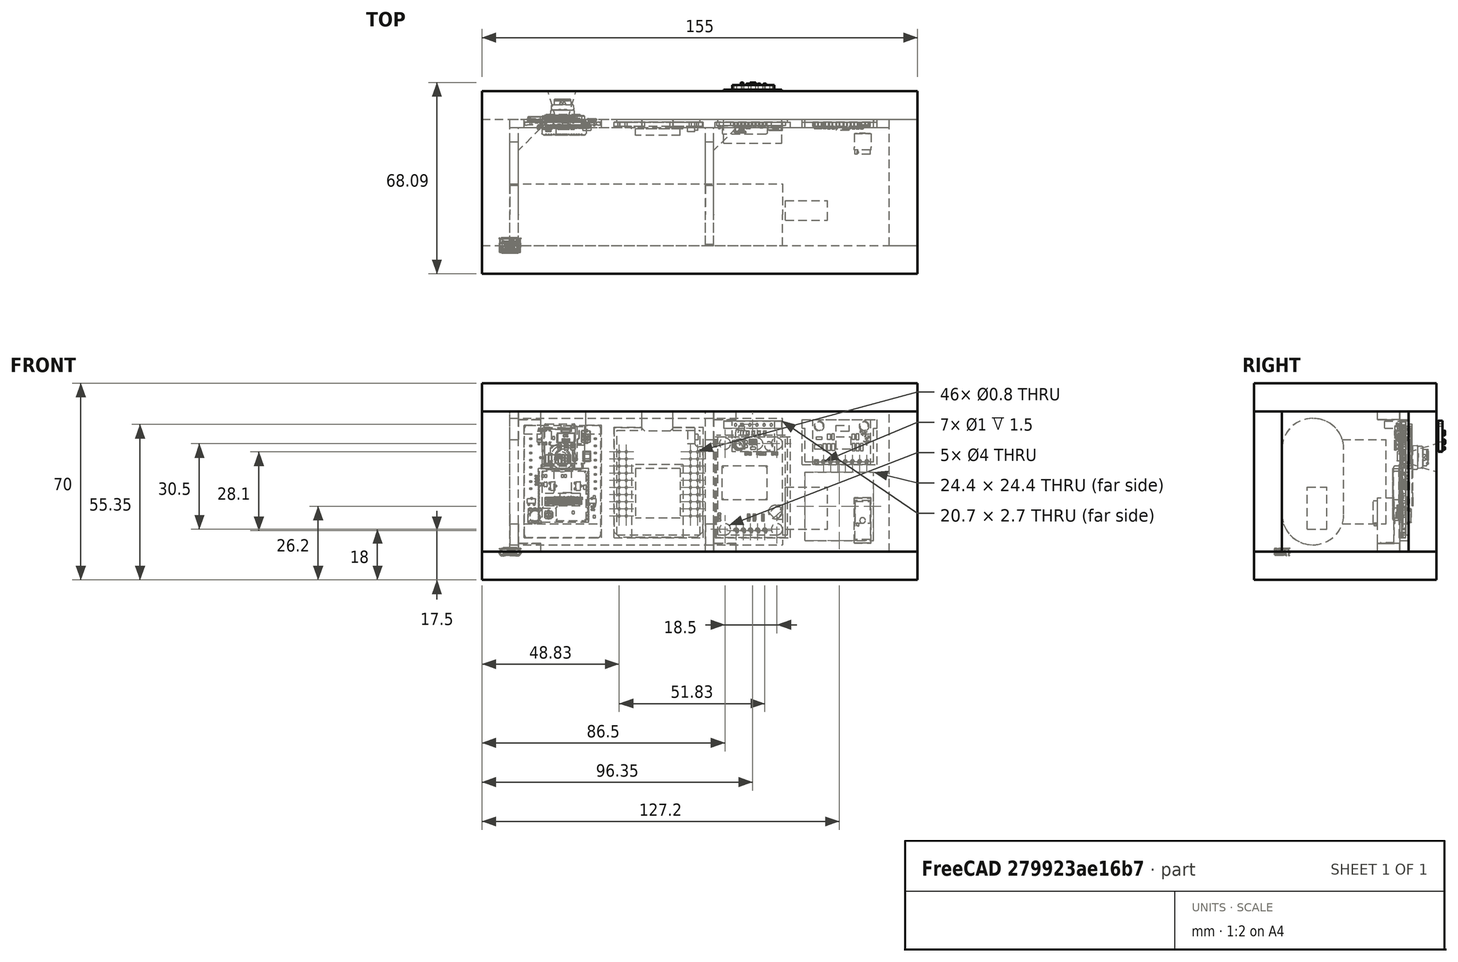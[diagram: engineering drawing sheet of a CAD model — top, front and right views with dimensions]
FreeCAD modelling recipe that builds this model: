
FCSTD DOCUMENT  (FreeCAD 0.18R4 (GitTag))
Label: fli3d chicken
License: All rights reserved
LicenseURL: http://en.wikipedia.org/wiki/All_rights_reserved
objects: Part::Feature×145, Part::Cylinder×138, Part::Cut×54, Part::Box×49, Part::Compound×15, Part::MultiFuse×13, Part::Chamfer×6, Part::Fillet×5, Mesh::Feature×4, App::Part×1, Part::Cone×1
note: 426 computed .brp shape members not serialized (recipe doc carries the construction recipe); baked Part::Feature solids carry a one-line shape summary decoded from their .brp

FEATURE [Part::Feature] Part__Feature183  label="pcb"
  shape: bbox 20.5 x 16 x 1.5 mm, 92 faces (baked)
FEATURE [Part::Feature] Part__Feature184  label="pcb001"
  shape: bbox 5.2 x 4.498 x 1 mm, 6 faces (baked)
FEATURE [Part::Feature] Part__Feature185  label="pcb002"
  shape: bbox 4.542 x 2.102 x 1.5 mm, 6 faces (baked)
FEATURE [Part::Feature] Part__Feature186  label="pcb003"
  shape: bbox 1.036 x 2.536 x 1 mm, 6 faces (baked)
FEATURE [Part::Feature] Part__Feature187  label="pcb004"
  shape: bbox 0.9209 x 2 x 1 mm, 6 faces (baked)
FEATURE [Part::Feature] Part__Feature188  label="pcb005"
  shape: bbox 1 x 2 x 1 mm, 6 faces (baked)
FEATURE [Part::Feature] Part__Feature189  label="pcb006"
  shape: bbox 1.036 x 2.536 x 1 mm, 6 faces (baked)
FEATURE [Part::Feature] Part__Feature190  label="pcb007"
  shape: bbox 1 x 2 x 1 mm, 6 faces (baked)
FEATURE [Part::Feature] Part__Feature191  label="pcb008"
  shape: bbox 2 x 1 x 1 mm, 6 faces (baked)
FEATURE [Part::Feature] Part__Feature192  label="pcb009"
  shape: bbox 1.036 x 2.536 x 1 mm, 6 faces (baked)
FEATURE [Part::Feature] Part__Feature193  label="pcb010"
  shape: bbox 1.036 x 2.536 x 1 mm, 6 faces (baked)
FEATURE [Part::Feature] Part__Feature194  label="pcb011"
  shape: bbox 0.9209 x 2 x 1 mm, 6 faces (baked)
FEATURE [Part::Feature] Part__Feature195  label="pcb012"
  shape: bbox 1.036 x 2.536 x 1 mm, 6 faces (baked)
FEATURE [Part::Feature] Part__Feature196  label="pcb013"
  shape: bbox 1.036 x 2.536 x 1 mm, 6 faces (baked)
FEATURE [Part::Feature] Part__Feature197  label="pcb014"
  shape: bbox 2.769 x 1.403 x 1 mm, 6 faces (baked)
FEATURE [Part::Feature] Part__Feature198  label="pcb015"
  shape: bbox 1.5 x 1.5 x 1.5 mm, 4 faces (baked)
FEATURE [Part::Feature] Part__Feature199  label="pcb016"
  shape: bbox 1.5 x 1.5 x 1.5 mm, 4 faces (baked)
FEATURE [Part::Feature] Part__Feature200  label="pcb017"
  shape: bbox 1.5 x 1.5 x 1.5 mm, 7 faces (baked)
FEATURE [Part::Feature] Part__Feature201  label="pcb018"
  shape: bbox 1.5 x 1.5 x 1.5 mm, 4 faces (baked)
FEATURE [Part::Feature] Part__Feature202  label="pcb019"
  shape: bbox 3.5 x 3.5 x 1.5 mm, 4 faces (baked)
FEATURE [Part::Feature] Part__Feature203  label="pcb020"
  shape: bbox 1.5 x 1.5 x 1.5 mm, 4 faces (baked)
FEATURE [Part::Feature] Part__Feature204  label="pcb021"
  shape: bbox 1.5 x 1.5 x 1.5 mm, 4 faces (baked)
FEATURE [Part::Feature] Part__Feature205  label="pcb022"
  shape: bbox 1.5 x 1.5 x 1.5 mm, 4 faces (baked)
FEATURE [Part::Feature] Part__Feature206  label="pcb023"
  shape: bbox 1.5 x 1.5 x 1.5 mm, 4 faces (baked)
FEATURE [Part::Feature] Part__Feature207  label="pcb024"
  shape: bbox 3.5 x 3.5 x 1.5 mm, 4 faces (baked)
FEATURE [Part::Feature] Part__Feature208  label="pcb025"
  shape: bbox 0.9 x 0.9 x 0.5 mm, 14 faces (baked)
FEATURE [Part::Feature] Part__Feature209  label="pcb026"
  shape: bbox 2.8 x 2.123 x 0.5 mm, 26 faces (baked)
FEATURE [Part::Feature] Part__Feature210  label="pcb027"
  shape: bbox 2.123 x 2.8 x 0.5 mm, 26 faces (baked)
FEATURE [Part::Feature] Part__Feature211  label="pcb028"
  shape: bbox 0.9 x 0.9 x 0.5 mm, 11 faces (baked)
FEATURE [Part::Compound] Compound019  label="MPU6050"
  Links = -> [Part__Feature183,Part__Feature184,Part__Feature185,Part__Feature186,Part__Feature187,Part__Feature188,Part__Feature189,Part__Feature190,Part__Feature191,Part__Feature192,Part__Feature193,Part__Feature194,Part__Feature195,Part__Feature196,Part__Feature197,Part__Feature198,Part__Feature199,Part__Feature200,Part__Feature201,Part__Feature202,Part__Feature203,Part__Feature204,Part__Feature205,+6 more]
  Placement = pos=(118,42.5,39) rot=(1,0,0;1.5708rad)
FEATURE [Part::Feature] Part__Feature251  label="Compound028"
  shape: bbox 0.9 x 0.55 x 1.7 mm, 36 faces (baked)
FEATURE [Part::Feature] Part__Feature252  label="Compound047"
  shape: bbox 0.9 x 0.55 x 1.7 mm, 36 faces (baked)
FEATURE [Part::Feature] Part__Feature253  label="Compound030"
  shape: bbox 1.7 x 0.9 x 0.9 mm, 34 faces (baked)
FEATURE [Part::Feature] Part__Feature255  label="Compound048"
  shape: bbox 0.9 x 0.55 x 1.7 mm, 36 faces (baked)
FEATURE [Part::Feature] Part__Feature257  label="Compound050"
  shape: bbox 2.518 x 0.974 x 2.018 mm, 265 faces (baked)
FEATURE [Part::Feature] Part__Feature258  label="Compound051"
  shape: bbox 0.9 x 0.9 x 1.7 mm, 34 faces (baked)
FEATURE [Part::Feature] Part__Feature259  label="Compound052"
  shape: bbox 0.9 x 0.55 x 1.7 mm, 36 faces (baked)
FEATURE [Part::Feature] Part__Feature262  label="Compound055"
  shape: bbox 15 x 1.57 x 11 mm, 14 faces (baked)
FEATURE [Part::Compound] Compound021  label="BMP280"
  Links = -> [Part__Feature262,Part__Feature255,Part__Feature258,Part__Feature259,Part__Feature257,Part__Feature252,Part__Feature251,Part__Feature253]
  Placement = pos=(90,80,45) rot=(0,1,0;3.14159rad)
FEATURE [Part::Feature] Part__Feature327  label="Pin Header 4 x 1 TH 2.54mm Pitch v033"
  Placement = pos=(4.72,-2.66216,2.20216) rot=(0.57735,0.57735,0.57735;4.18879rad)
  shape: bbox 0.635 x 11.43 x 0.635 mm, 14 faces (baked)
FEATURE [Mesh::Feature] __54_pin_header008  label="2.54_pin_header008"
  Placement = pos=(8.5,27.2,-0.8) rot=(0,0,1;0rad)
FEATURE [Part::Feature] Part__Feature328  label="Pin Header 4 x 1 TH 2.54mm Pitch v034"
  Placement = pos=(14.89,-2.66216,25.2022) rot=(0.57735,0.57735,0.57735;4.18879rad)
  shape: bbox 0.635 x 11.43 x 0.635 mm, 14 faces (baked)
FEATURE [Part::Feature] Part__Feature329  label="Pin Header 4 x 1 TH 2.54mm Pitch v035"
  Placement = pos=(4.72,-2.66216,2.20216) rot=(0.57735,0.57735,0.57735;4.18879rad)
  shape: bbox 0.635 x 11.43 x 0.635 mm, 14 faces (baked)
FEATURE [Part::Feature] Part__Feature330  label="Pin Header 4 x 1 TH 2.54mm Pitch v036"
  Placement = pos=(14.89,-2.66216,25.2022) rot=(0.57735,0.57735,0.57735;4.18879rad)
  shape: bbox 0.635 x 11.43 x 0.635 mm, 14 faces (baked)
FEATURE [Part::Feature] Part__Feature331  label="Pin Header 4 x 1 TH 2.54mm Pitch v037"
  Placement = pos=(4.72,-2.66216,2.20216) rot=(0.57735,0.57735,0.57735;4.18879rad)
  shape: bbox 0.635 x 11.43 x 0.635 mm, 14 faces (baked)
FEATURE [Part::Feature] Part__Feature332  label="Pin Header 4 x 1 TH 2.54mm Pitch v038"
  Placement = pos=(14.883,-2.66216,2.20216) rot=(0.57735,0.57735,0.57735;4.18879rad)
  shape: bbox 0.635 x 11.43 x 0.635 mm, 14 faces (baked)
FEATURE [Part::Feature] Part__Feature333  label="Pin Header 4 x 1 TH 2.54mm Pitch v039"
  Placement = pos=(14.89,-2.66216,25.2022) rot=(0.57735,0.57735,0.57735;4.18879rad)
  shape: bbox 0.635 x 11.43 x 0.635 mm, 14 faces (baked)
FEATURE [Part::Feature] Part__Feature334  label="Pin Header 4 x 1 TH 2.54mm Pitch v040"
  Placement = pos=(14.89,-2.66216,25.2022) rot=(0.57735,0.57735,0.57735;4.18879rad)
  shape: bbox 0.635 x 11.43 x 0.635 mm, 14 faces (baked)
FEATURE [Part::Feature] Part__Feature335  label="Pin Header 4 x 1 TH 2.54mm Pitch v041"
  Placement = pos=(4.72,-2.66216,2.20216) rot=(0.57735,0.57735,0.57735;4.18879rad)
  shape: bbox 0.635 x 11.43 x 0.635 mm, 14 faces (baked)
FEATURE [Part::Feature] Part__Feature336  label="Pin Header 4 x 1 TH 2.54mm Pitch v042"
  Placement = pos=(4.71,-2.66216,25.2022) rot=(-0.57735,-0.57735,-0.57735;2.0944rad)
  shape: bbox 0.635 x 11.43 x 0.635 mm, 14 faces (baked)
FEATURE [Part::Feature] Part__Feature337  label="Pin Header 4 x 1 TH 2.54mm Pitch v043"
  Placement = pos=(4.71,-2.66216,25.2022) rot=(-0.57735,-0.57735,-0.57735;2.0944rad)
  shape: bbox 0.635 x 11.43 x 0.635 mm, 14 faces (baked)
FEATURE [Part::Feature] Part__Feature338  label="Pin Header 4 x 1 TH 2.54mm Pitch v044"
  Placement = pos=(14.883,-2.66216,2.20216) rot=(0.57735,0.57735,0.57735;4.18879rad)
  shape: bbox 0.635 x 11.43 x 0.635 mm, 14 faces (baked)
FEATURE [Part::Feature] Part__Feature339  label="Pin Header 4 x 1 TH 2.54mm Pitch v045"
  Placement = pos=(14.883,-2.66216,2.20216) rot=(0.57735,0.57735,0.57735;4.18879rad)
  shape: bbox 0.635 x 11.43 x 0.635 mm, 14 faces (baked)
FEATURE [Part::Feature] Part__Feature340  label="Pin Header 4 x 1 TH 2.54mm Pitch v046"
  Placement = pos=(14.883,-2.66216,2.20216) rot=(0.57735,0.57735,0.57735;4.18879rad)
  shape: bbox 0.635 x 11.43 x 0.635 mm, 14 faces (baked)
FEATURE [Part::Feature] Part__Feature341  label="u005"
  Placement = pos=(30.5196,-1.14548,7.21031) rot=(1,0,0;3.14159rad)
  shape: bbox 1.8 x 0.165 x 0.4527 mm, 9 faces (baked)
FEATURE [Part::Feature] Part__Feature342  label="u006"
  Placement = pos=(30.5196,-1.14548,7.21031) rot=(1,0,0;3.14159rad)
  shape: bbox 0.5465 x 0.165 x 0.6 mm, 7 faces (baked)
FEATURE [Part::Feature] Part__Feature343  label="switch-3x4x2mm - 2 Pad v002"
  Placement = pos=(4,0.684989,21.7704) rot=(1,0,0;1.5708rad)
  shape: bbox 5.004 x 1.93 x 2.997 mm, 237 faces (baked)
FEATURE [Part::Feature] Part__Feature344  label="Pin Header 4 x 1 TH 2.54mm Pitch v047"
  Placement = pos=(4.71,-2.66216,25.2022) rot=(-0.57735,-0.57735,-0.57735;2.0944rad)
  shape: bbox 0.635 x 11.43 x 0.635 mm, 14 faces (baked)
FEATURE [Part::Feature] Part__Feature345  label="nano - reg001"
  Placement = pos=(4.45,-0.0046987,14.7657) rot=(-0.707107,0,0.707107;3.14159rad)
  shape: bbox 8.304 x 1.695 x 6.504 mm, 194 faces (baked)
FEATURE [Part::Feature] Part__Feature346  label="Pin Header 4 x 1 TH 2.54mm Pitch v048"
  Placement = pos=(4.71,-2.66216,25.2022) rot=(-0.57735,-0.57735,-0.57735;2.0944rad)
  shape: bbox 0.635 x 11.43 x 0.635 mm, 14 faces (baked)
FEATURE [Part::Compound] Compound121  label="pins001"
  Links = -> [Part__Feature344,Part__Feature340,Part__Feature332,Part__Feature337,Part__Feature334,Part__Feature346,Part__Feature339,Part__Feature330,Part__Feature328,Part__Feature338,Part__Feature335,Part__Feature336,Part__Feature329,Part__Feature327,Part__Feature331,Part__Feature333]
FEATURE [Part::Feature] Part__Feature347  label="u007"
  Placement = pos=(30.5196,-1.14548,7.21031) rot=(1,0,0;3.14159rad)
  shape: bbox 1.8 x 0.165 x 0.4527 mm, 9 faces (baked)
FEATURE [Part::Feature] Part__Feature348  label="u008"
  Placement = pos=(30.5196,-1.14548,7.21031) rot=(1,0,0;3.14159rad)
  shape: bbox 2.616 x 1.25 x 2.633 mm, 39 faces (baked)
FEATURE [Part::Feature] Part__Feature349  label="u009"
  Placement = pos=(30.5196,-1.14548,7.21031) rot=(1,0,0;3.14159rad)
  shape: bbox 0.5465 x 0.165 x 0.6 mm, 7 faces (baked)
FEATURE [Part::Feature] Part__Feature350  label="SOLID004"
  Placement = pos=(15.3712,-0.145481,22.8712) rot=(0.707107,0,-0.707107;3.14159rad)
  shape: bbox 19.24 x 3.435 x 18.07 mm, 845 faces (baked)
FEATURE [Part::Feature] Part__Feature351  label="capacitor-CAPM-TANTB-YL v004"
  Placement = pos=(11,0.104975,22.105) rot=(1,0,0;1.5708rad)
  shape: bbox 3.446 x 2.076 x 3.006 mm, 54 faces (baked)
FEATURE [Part::Feature] Part__Feature352  label="capacitor-CAPM-TANTB-YL v005"
  Placement = pos=(11,0.104975,22.105) rot=(1,0,0;1.5708rad)
  shape: bbox 1 x 1.13 x 2.2 mm, 18 faces (baked)
FEATURE [Part::Feature] Part__Feature353  label="capacitor-CAPM-TANTB-YL v006"
  Placement = pos=(11,0.104975,22.105) rot=(1,0,0;1.5708rad)
  shape: bbox 1 x 1.13 x 2.2 mm, 18 faces (baked)
FEATURE [Part::Feature] Part__Feature354  label="resistor-NTC-0402-T0.6 v021"
  Placement = pos=(10.2,0,12.3) rot=(0,1,0;1.5708rad)
  shape: bbox 0.6 x 0.55 x 1.1 mm, 42 faces (baked)
FEATURE [Part::Feature] Part__Feature355  label="Component009"
  Placement = pos=(4,-1.3e-14,7) rot=(0.57735,-0.57735,0.57735;2.0944rad)
  shape: bbox 1 x 1.05 x 0.4 mm, 14 faces (baked)
FEATURE [Part::Feature] Part__Feature356  label="Component5(Mirror)004"
  Placement = pos=(4,-1.2e-14,8.27) rot=(0.57735,0.57735,0.57735;4.18879rad)
  shape: bbox 1 x 1.05 x 0.4 mm, 14 faces (baked)
FEATURE [Part::Feature] Part__Feature357  label="icbody001"
  Placement = pos=(4,-1.3e-14,7) rot=(0.57735,-0.57735,0.57735;2.0944rad)
  shape: bbox 3.9 x 1.45 x 4.9 mm, 50 faces (baked)
FEATURE [Part::Feature] Part__Feature358  label="Component010"
  Placement = pos=(4,-1.5e-14,5.73) rot=(0.57735,-0.57735,0.57735;2.0944rad)
  shape: bbox 1 x 1.05 x 0.4 mm, 14 faces (baked)
FEATURE [Part::Feature] Part__Feature359  label="Component5(Mirror)005"
  Placement = pos=(4,-1.3e-14,7) rot=(0.57735,0.57735,0.57735;4.18879rad)
  shape: bbox 1 x 1.05 x 0.4 mm, 14 faces (baked)
FEATURE [Part::Feature] Part__Feature360  label="Component5(Mirror)006"
  Placement = pos=(4,-1.6e-14,4.46) rot=(0.57735,0.57735,0.57735;4.18879rad)
  shape: bbox 1 x 1.05 x 0.4 mm, 14 faces (baked)
FEATURE [Part::Feature] Part__Feature361  label="Component011"
  Placement = pos=(4,-1.6e-14,4.46) rot=(0.57735,-0.57735,0.57735;2.0944rad)
  shape: bbox 1 x 1.05 x 0.4 mm, 14 faces (baked)
FEATURE [Part::Feature] Part__Feature362  label="Component5(Mirror)007"
  Placement = pos=(4,-1.5e-14,5.73) rot=(0.57735,0.57735,0.57735;4.18879rad)
  shape: bbox 1 x 1.05 x 0.4 mm, 14 faces (baked)
FEATURE [Part::Feature] Part__Feature363  label="Fusion054"
  Placement = pos=(12,-5e-15,18) rot=(0.57735,-0.57735,0.57735;2.0944rad)
  shape: bbox 0.8 x 0.5 x 1.6 mm, 25 faces (baked)
FEATURE [Part::Feature] Part__Feature364  label="Fillet034"
  Placement = pos=(12,-5e-15,18) rot=(0.57735,-0.57735,0.57735;2.0944rad)
  shape: bbox 0.8 x 0.3 x 1.2 mm, 18 faces (baked)
FEATURE [Part::Feature] Part__Feature365  label="resistor-NTC-0402-T0.6 v022"
  Placement = pos=(12.2,0,15.8) rot=(0,1,0;1.5708rad)
  shape: bbox 0.6 x 0.55 x 1.1 mm, 42 faces (baked)
FEATURE [Part::Feature] Part__Feature366  label="Component012"
  Placement = pos=(4,-1.2e-14,8.27) rot=(0.57735,-0.57735,0.57735;2.0944rad)
  shape: bbox 1 x 1.05 x 0.4 mm, 14 faces (baked)
FEATURE [Part::Feature] Part__Feature367  label="smd-transistor-SOT23-3 v017"
  Placement = pos=(27,1.05803,23.942) rot=(-1,0,0;1.5708rad)
  shape: bbox 0.6498 x 0.8933 x 0.6 mm, 7 faces (baked)
FEATURE [Part::Feature] Part__Feature368  label="smd-transistor-SOT23-3 v018"
  Placement = pos=(27,1.05803,2.44197) rot=(-1,0,0;1.5708rad)
  shape: bbox 0.6498 x 0.8933 x 0.6 mm, 7 faces (baked)
FEATURE [Part::Feature] Part__Feature369  label="resistor-NTC-0402-T0.6 v023"
  Placement = pos=(25.5,0,24.5) rot=(0,0,1;0rad)
  shape: bbox 1.1 x 0.55 x 0.6 mm, 42 faces (baked)
FEATURE [Part::Feature] Part__Feature370  label="resistor-NTC-0402-T0.6 v024"
  Placement = pos=(28.5,0,24.5) rot=(0,0,1;0rad)
  shape: bbox 1.1 x 0.55 x 0.6 mm, 42 faces (baked)
FEATURE [Part::Feature] Part__Feature371  label="smd-transistor-SOT23-3 v019"
  Placement = pos=(27,1.05803,2.44197) rot=(-1,0,0;1.5708rad)
  shape: bbox 0.6498 x 0.8933 x 0.6 mm, 7 faces (baked)
FEATURE [Part::Feature] Part__Feature372  label="resistor-NTC-0402-T0.6 v025"
  Placement = pos=(32.5,0,24.5) rot=(0,0,1;0rad)
  shape: bbox 1.1 x 0.55 x 0.6 mm, 42 faces (baked)
FEATURE [Part::Feature] Part__Feature373  label="smd-transistor-SOT23-3 v020"
  Placement = pos=(27,1.05803,2.44197) rot=(-1,0,0;1.5708rad)
  shape: bbox 0.6498 x 0.8933 x 0.6 mm, 7 faces (baked)
FEATURE [Part::Feature] Part__Feature374  label="smd-transistor-SOT23-3 v021"
  Placement = pos=(27,1.05803,2.44197) rot=(-1,0,0;1.5708rad)
  shape: bbox 1.651 x 1.1 x 3 mm, 34 faces (baked)
FEATURE [Part::Feature] Part__Feature375  label="resistor-NTC-0402-T0.6 v026"
  Placement = pos=(4.5,0,10.6) rot=(0,1,0;3.14159rad)
  shape: bbox 1.1 x 0.55 x 0.6 mm, 42 faces (baked)
FEATURE [Part::Feature] Part__Feature376  label="smd-transistor-SOT23-3 v022"
  Placement = pos=(27,1.05803,23.942) rot=(-1,0,0;1.5708rad)
  shape: bbox 0.6498 x 0.8933 x 0.6 mm, 7 faces (baked)
FEATURE [Part::Feature] Part__Feature377  label="smd-transistor-SOT23-3 v023"
  Placement = pos=(27,1.05803,23.942) rot=(-1,0,0;1.5708rad)
  shape: bbox 0.6498 x 0.8933 x 0.6 mm, 7 faces (baked)
FEATURE [Part::Feature] Part__Feature378  label="resistor-NTC-0805-T1.3 v002"
  Placement = pos=(10.35,0,14.65) rot=(0,1,0;1.5708rad)
  shape: bbox 1.3 x 1.4 x 2.2 mm, 42 faces (baked)
FEATURE [Part::Feature] Part__Feature379  label="resistor-NTC-0402-T0.6 v027"
  Placement = pos=(11.2,0,5.97136) rot=(0,1,0;1.5708rad)
  shape: bbox 0.6 x 0.55 x 1.1 mm, 42 faces (baked)
FEATURE [Part::Feature] Part__Feature380  label="resistor-NTC-0402-T0.6 v028"
  Placement = pos=(17.7,1,4.3) rot=(0,1,0;1.5708rad)
  shape: bbox 0.6 x 0.55 x 1.1 mm, 42 faces (baked)
FEATURE [Part::Feature] Part__Feature381  label="resistor-NTC-0402-T0.6 v029"
  Placement = pos=(18.7,1,4.3) rot=(0,1,0;1.5708rad)
  shape: bbox 0.6 x 0.55 x 1.1 mm, 42 faces (baked)
FEATURE [Part::Feature] Part__Feature382  label="resistor-NTC-0402-T0.6 v030"
  Placement = pos=(21,1,5.2) rot=(0,0,1;0rad)
  shape: bbox 1.1 x 0.55 x 0.6 mm, 42 faces (baked)
FEATURE [Part::Feature] Part__Feature383  label="resistor-NTC-0402-T0.6 v031"
  Placement = pos=(29.3,1,24.3) rot=(0,-1,0;1.5708rad)
  shape: bbox 0.6 x 0.55 x 1.1 mm, 42 faces (baked)
FEATURE [Part::Feature] Part__Feature384  label="smd-transistor-SOT23-3 v024"
  Placement = pos=(27,1.05803,23.942) rot=(-1,0,0;1.5708rad)
  shape: bbox 1.651 x 1.1 x 3 mm, 34 faces (baked)
FEATURE [Part::Feature] Part__Feature385  label="resistor-NTC-0402-T0.6 v032"
  Placement = pos=(30.3,1,24.3) rot=(0,-1,0;1.5708rad)
  shape: bbox 0.6 x 0.55 x 1.1 mm, 42 faces (baked)
FEATURE [Part::Feature] Part__Feature386  label="resistor-NTC-0402-T0.6 v033"
  Placement = pos=(19.7,1,4.3) rot=(0,1,0;1.5708rad)
  shape: bbox 0.6 x 0.55 x 1.1 mm, 42 faces (baked)
FEATURE [Part::Feature] Part__Feature387  label="resistor-NTC-0402-T0.6 v034"
  Placement = pos=(20.7,1,4.3) rot=(0,1,0;1.5708rad)
  shape: bbox 0.6 x 0.55 x 1.1 mm, 42 faces (baked)
FEATURE [Part::Feature] Part__Feature388  label="resistor-NTC-0402-T0.6 v035"
  Placement = pos=(18,1,6.2) rot=(0,0,1;0rad)
  shape: bbox 1.1 x 0.55 x 0.6 mm, 42 faces (baked)
FEATURE [Part::Feature] Part__Feature389  label="resistor-NTC-0402-T0.6 v036"
  Placement = pos=(18,1,7.2) rot=(0,0,1;0rad)
  shape: bbox 1.1 x 0.55 x 0.6 mm, 42 faces (baked)
FEATURE [Part::Feature] Part__Feature390  label="capacitor-CAPC-0603-T0.9-BN v003"
  Placement = pos=(21,1,7) rot=(0,0,1;0rad)
  shape: bbox 1.7 x 0.9 x 0.9 mm, 42 faces (baked)
FEATURE [Part::Feature] Part__Feature391  label="LED SMD 5050 White v002"
  Placement = pos=(30,1.2963,2.10027) rot=(-1,0,0;1.5708rad)
  shape: bbox 5.4 x 1.62 x 5 mm, 76 faces (baked)
FEATURE [Part::Feature] Part__Feature392  label="resistor-NTC-0402-T0.6 v037"
  Placement = pos=(31,1,17) rot=(0,0,1;0rad)
  shape: bbox 1.1 x 0.55 x 0.6 mm, 42 faces (baked)
FEATURE [Part::Feature] Part__Feature393  label="smd-transistor-SOT23-3 v025"
  Placement = pos=(21.5739,1.05803,19.0158) rot=(-0.57735,0.57735,0.57735;2.0944rad)
  shape: bbox 0.6 x 0.8933 x 0.6498 mm, 7 faces (baked)
FEATURE [Part::Feature] Part__Feature394  label="smd-transistor-SOT23-3 v026"
  Placement = pos=(21.5739,1.05803,19.0158) rot=(-0.57735,0.57735,0.57735;2.0944rad)
  shape: bbox 0.6 x 0.8933 x 0.6498 mm, 7 faces (baked)
FEATURE [Part::Feature] Part__Feature395  label="connector smd usl00-20l_p0-4_l12-6_w2-75 v002"
  Placement = pos=(26.791,1,14.009) rot=(0,1,0;1.5708rad)
  shape: bbox 3.1 x 1 x 12.6 mm, 645 faces (baked)
FEATURE [Part::Feature] Part__Feature396  label="smd-transistor-SOT23-3 v027"
  Placement = pos=(21.5739,1.05803,19.0158) rot=(-0.57735,0.57735,0.57735;2.0944rad)
  shape: bbox 3 x 1.1 x 1.651 mm, 34 faces (baked)
FEATURE [Part::Feature] Part__Feature397  label="resistor-NTC-0402-T0.6 v038"
  Placement = pos=(18,1,14.2) rot=(0,0,1;0rad)
  shape: bbox 1.1 x 0.55 x 0.6 mm, 42 faces (baked)
FEATURE [Part::Feature] Part__Feature398  label="capacitor-CAPC-0603-T0.9-BN v004"
  Placement = pos=(22,1,21) rot=(0,0,1;0rad)
  shape: bbox 1.7 x 0.9 x 0.9 mm, 42 faces (baked)
FEATURE [Part::Feature] Part__Feature399  label="smd-transistor-SOT23-3 v028"
  Placement = pos=(21.5739,1.05803,10.0158) rot=(-0.57735,0.57735,0.57735;2.0944rad)
  shape: bbox 0.6 x 0.8933 x 0.6498 mm, 7 faces (baked)
FEATURE [Part::Feature] Part__Feature400  label="smd-transistor-SOT23-3 v029"
  Placement = pos=(21.5739,1.05803,10.0158) rot=(-0.57735,0.57735,0.57735;2.0944rad)
  shape: bbox 0.6 x 0.8933 x 0.6498 mm, 7 faces (baked)
FEATURE [Part::Feature] Part__Feature401  label="smd-transistor-SOT23-3 v030"
  Placement = pos=(21.5739,1.05803,10.0158) rot=(-0.57735,0.57735,0.57735;2.0944rad)
  shape: bbox 3 x 1.1 x 1.651 mm, 34 faces (baked)
FEATURE [Part::Feature] Part__Feature402  label="resistor-NTC-0402-T0.6 v039"
  Placement = pos=(21,1,6) rot=(0,0,1;0rad)
  shape: bbox 1.1 x 0.55 x 0.6 mm, 42 faces (baked)
FEATURE [Part::Feature] Part__Feature403  label="smd-transistor-SOT23-3 v031"
  Placement = pos=(21.5739,1.05803,19.0158) rot=(-0.57735,0.57735,0.57735;2.0944rad)
  shape: bbox 0.6 x 0.8933 x 0.6498 mm, 7 faces (baked)
FEATURE [Part::Feature] Part__Feature404  label="smd-transistor-SOT23-3 v032"
  Placement = pos=(21.5739,1.05803,10.0158) rot=(-0.57735,0.57735,0.57735;2.0944rad)
  shape: bbox 0.6 x 0.8933 x 0.6498 mm, 7 faces (baked)
FEATURE [Part::Feature] Part__Feature405  label="resistor-NTC-0402-T0.6 v040"
  Placement = pos=(18,1,13.2) rot=(0,0,1;0rad)
  shape: bbox 1.1 x 0.55 x 0.6 mm, 42 faces (baked)
FEATURE [Part::Feature] Part__Feature406  label="Micro SD-Card v010"
  Placement = pos=(7,2.64,12.5) rot=(0,0,1;0rad)
  shape: bbox 3.1 x 0.01 x 0.95 mm, 10 faces (baked)
FEATURE [Part::Feature] Part__Feature407  label="Micro SD-Card v011"
  Placement = pos=(7,2.64,12.5) rot=(0,0,1;0rad)
  shape: bbox 3.1 x 0.01 x 0.95 mm, 10 faces (baked)
FEATURE [Part::Feature] Part__Feature408  label="Micro SD-Card v012"
  Placement = pos=(7,2.64,12.5) rot=(0,0,1;0rad)
  shape: bbox 3.1 x 0.01 x 0.95 mm, 10 faces (baked)
FEATURE [Part::Feature] Part__Feature409  label="Micro SD-Card v013"
  Placement = pos=(7,2.64,12.5) rot=(0,0,1;0rad)
  shape: bbox 3.1 x 0.01 x 0.95 mm, 10 faces (baked)
FEATURE [Part::Feature] Part__Feature410  label="Micro SD-Card v014"
  Placement = pos=(7,2.64,12.5) rot=(0,0,1;0rad)
  shape: bbox 3.1 x 0.01 x 0.95 mm, 10 faces (baked)
FEATURE [Part::Feature] Part__Feature411  label="User Library-ov9655_ov9655_flex_reinf001"
  Placement = pos=(24.1466,3.31977,13.5126) rot=(0.57735,-0.57735,-0.57735;4.18879rad)
  shape: bbox 4.5 x 0.25 x 12.5 mm, 6 faces (baked)
FEATURE [Part::Feature] Part__Feature412  label="AMS1118"
  Placement = pos=(26.2661,1.87,19.328) rot=(0,0,1;0rad)
FEATURE [Part::Feature] Part__Feature413  label="User Library-ov9655_ov9655_flex_pcb001"
  Placement = pos=(24.1466,3.31977,13.5126) rot=(0.57735,-0.57735,-0.57735;4.18879rad)
  shape: bbox 21.5 x 0.12 x 12.5 mm, 20 faces (baked)
FEATURE [Part::Feature] Part__Feature414  label="sdreader001"
  Placement = pos=(15.4256,-0.2,14.568) rot=(-1,0,0;1.5708rad)
  shape: bbox 15 x 2.025 x 16 mm, 54 faces (baked)
FEATURE [Part::Feature] Part__Feature415  label="Micro SD-Card v015"
  Placement = pos=(7,2.64,12.5) rot=(0,0,1;0rad)
  shape: bbox 3.35 x 0.01 x 0.95 mm, 10 faces (baked)
FEATURE [Part::Feature] Part__Feature416  label="Micro SD-Card v016"
  Placement = pos=(7,2.64,12.5) rot=(0,0,1;0rad)
  shape: bbox 3.35 x 0.01 x 0.95 mm, 10 faces (baked)
FEATURE [Part::Feature] Part__Feature417  label="Micro SD-Card v017"
  Placement = pos=(7,2.64,12.5) rot=(0,0,1;0rad)
  shape: bbox 15 x 1 x 11.09 mm, 23 faces (baked)
FEATURE [Part::Feature] Part__Feature418  label="Micro SD-Card v018"
  Placement = pos=(7,2.64,12.5) rot=(0,0,1;0rad)
  shape: bbox 3.1 x 0.01 x 0.95 mm, 10 faces (baked)
FEATURE [Part::Feature] Part__Feature419  label="User Library-ov9655_ov9655_body001"
  Placement = pos=(24.1466,3.31977,13.5126) rot=(0.57735,-0.57735,-0.57735;4.18879rad)
  shape: bbox 8.847 x 6.041 x 8.847 mm, 59 faces (baked)
FEATURE [Part::Feature] Part__Feature420  label="User Library-ov9655_ov9655_lens001"
  Placement = pos=(24.1466,3.31977,13.5126) rot=(0.57735,-0.57735,-0.57735;4.18879rad)
  shape: bbox 2 x 1.43 x 2 mm, 3 faces (baked)
FEATURE [Part::Feature] Part__Feature421  label="SOLID005"
  shape: bbox 40 x 1 x 27 mm, 10 faces (baked)
FEATURE [Part::Cut] Cut143  label="PCB004"
  Base = -> Part__Feature421
  Tool = -> Compound121
FEATURE [Part::Feature] Part__Feature422  label="User Library-ov9655_ov9655_back_panel001"
  Placement = pos=(24.1466,3.31977,13.5126) rot=(0.57735,-0.57735,-0.57735;4.18879rad)
  shape: bbox 8.5 x 0.25 x 8.5 mm, 10 faces (baked)
FEATURE [Part::Compound] Compound122  label="ESP32-CAM001"
  Links = -> [Cut143,Part__Feature369,Part__Feature361,Part__Feature418,Part__Feature363,Part__Feature390,Part__Feature414,Part__Feature356,Part__Feature382,Part__Feature392,Part__Feature408,Part__Feature365,Part__Feature351,Part__Feature345,Part__Feature398,Part__Feature384,Part__Feature359,Part__Feature404,Part__Feature354,Part__Feature371,Part__Feature352,Part__Feature420,Part__Feature405,Part__Feature402,+56 more]
  Placement = pos=(5.2,43,45) rot=(0,1,0;1.5708rad)
FEATURE [Part::Feature] Part__Feature423  label="SOLID006"
  Placement = pos=(0,0,0) rot=(-1,0,0;1.5708rad)
  shape: bbox 7.981 x 5.431 x 2.941 mm, 406 faces (baked)
FEATURE [App::Part] _73460003  label="micro USB002"
  Group = -> [Part__Feature423]
  Origin = -> Origin002
  Placement = pos=(2,16,-1.3) rot=(0,0,1;1.5708rad)
FEATURE [Part::Feature] Part__Feature424  label="GPS_res475"
  Placement = pos=(-13.49,1.3,-12.319) rot=(0,-1,0;1.5708rad)
  shape: bbox 1.02 x 0.6154 x 2.362 mm, 138 faces, 4 solids (baked)
FEATURE [Part::Feature] Part__Feature425  label="GPS_res476"
  Placement = pos=(-16.49,1.3,-12.319) rot=(0,-1,0;1.5708rad)
  shape: bbox 1.02 x 0.6154 x 2.362 mm, 138 faces, 4 solids (baked)
FEATURE [Part::Feature] Part__Feature426  label="GPS_battery001"
  Placement = pos=(-14.7943,1.29979,13.0331) rot=(-0.850961,-0.371393,-0.371393;1.73149rad)
  shape: bbox 5.675 x 1.701 x 5.675 mm, 36 faces (baked)
FEATURE [Part::Feature] Part__Feature427  label="GPS_res477"
  Placement = pos=(-11.4616,1.3,-12.319) rot=(0,1,0;1.5708rad)
  shape: bbox 1.02 x 0.6154 x 2.362 mm, 124 faces, 4 solids (baked)
FEATURE [Part::Feature] Part__Feature428  label="GPS_res478"
  Placement = pos=(-20.7044,1.68325,10.5205) rot=(0,0,1;0rad)
  shape: bbox 2.362 x 0.6154 x 1.02 mm, 124 faces, 4 solids (baked)
FEATURE [Part::Feature] Part__Feature429  label="GPS_res479"
  Placement = pos=(-11.2066,1.68325,10.5205) rot=(0,0,1;0rad)
  shape: bbox 2.362 x 0.6154 x 1.02 mm, 124 faces, 4 solids (baked)
FEATURE [Part::Feature] Part__Feature430  label="GPS_cap001"
  Placement = pos=(-1.008,1.35775,-12.1193) rot=(0,-1,0;1.5708rad)
  shape: bbox 1.226 x 0.955 x 3.329 mm, 56 faces (baked)
FEATURE [Part::Feature] Part__Feature431  label="GPS_led001"
  Placement = pos=(-15.9936,1.3,10.5305) rot=(0,0,1;0rad)
  shape: bbox 3.551 x 0.7528 x 1.711 mm, 57 faces, 2 solids (baked)
FEATURE [Part::Box] Box226  label="Cube206"
  AttacherType = Attacher::AttachEngine3D
  Height = 1.5
  Length = 39
  Width = 31.4
FEATURE [Part::Chamfer] Chamfer047  label="Chamfer066"
  Base = -> Box226
  Edges = 2 edges r=2: [Edge5,Edge7]
FEATURE [Part::Box] Box227  label="Cube207"
  AttacherType = Attacher::AttachEngine3D
  Height = 1.5
  Length = 6.7
  Width = 2.8
FEATURE [Part::Fillet] Fillet029  label="Fillet035"
  Base = -> Box227
  Edges = 1 edges r=1.5: [Edge7]
FEATURE [Part::Box] Box228  label="Cube208"
  AttacherType = Attacher::AttachEngine3D
  Height = 1.5
  Length = 1.1
  Placement = pos=(0,10.5,0) rot=(0,0,1;0rad)
  Width = 11
FEATURE [Part::Chamfer] Chamfer048
  Base = -> Box228
  Edges = 2 edges r=1: [Edge5,Edge7]
FEATURE [Part::MultiFuse] Fusion061
  Shapes = -> [Chamfer048,Fillet029]
FEATURE [Part::Box] Box229  label="Antenna002"
  AttacherType = Attacher::AttachEngine3D
  Height = 0.9
  Length = 26
  Placement = pos=(13.1,7,-0.9) rot=(0,0,1;0rad)
  Width = 18.2
FEATURE [Part::Box] Box230  label="ESP033"
  AttacherType = Attacher::AttachEngine3D
  Height = 2.2
  Length = 17.6
  Placement = pos=(14.5,8,-3.2) rot=(0,0,1;0rad)
  Width = 15.8
FEATURE [Part::Cut] Cut160  label="PCB005"
  Base = -> Chamfer047
  Tool = -> Fusion061
FEATURE [Mesh::Feature] __54_pin_header009  label="2.54_pin_header009"
  Placement = pos=(8.5,1.7,-0.8) rot=(0,0,1;0rad)
FEATURE [Mesh::Feature] __54_pin_header010  label="2.54_pin_header010"
  Placement = pos=(21.2,1.7,-0.8) rot=(0,0,1;0rad)
FEATURE [Part::Box] Box231  label="Cube209"
  AttacherType = Attacher::AttachEngine3D
  Height = 1
  Length = 2
  Placement = pos=(2.3,1.6,-1.5) rot=(0,0,1;0rad)
  Width = 1.2
FEATURE [Part::Cylinder] Cylinder254
  Angle = 360
  AttacherType = Attacher::AttachEngine3D
  Height = 1.5
  Radius = 0.9
FEATURE [Part::Cylinder] Cylinder255
  Angle = 360
  AttacherType = Attacher::AttachEngine3D
  Height = 1.5
  Radius = 0.4
FEATURE [Part::Cylinder] Cylinder256
  Angle = 360
  AttacherType = Attacher::AttachEngine3D
  Height = 1.5
  Radius = 0.9
FEATURE [Part::Cut] Cut158
  Base = -> Cylinder256
  Tool = -> Cylinder255
FEATURE [Part::Box] Box232  label="Cube210"
  AttacherType = Attacher::AttachEngine3D
  Height = 2
  Length = 4.7
  Placement = pos=(1,2.8,-2) rot=(0,0,1;0rad)
  Width = 2.5
FEATURE [Part::Cylinder] Cylinder257
  Angle = 360
  AttacherType = Attacher::AttachEngine3D
  Height = 1.5
  Radius = 0.4
FEATURE [Part::Cylinder] Cylinder258
  Angle = 360
  AttacherType = Attacher::AttachEngine3D
  Height = 1.5
  Radius = 0.4
FEATURE [Part::Cylinder] Cylinder259
  Angle = 360
  AttacherType = Attacher::AttachEngine3D
  Height = 1.5
  Radius = 0.4
FEATURE [Part::Cylinder] Cylinder260
  Angle = 360
  AttacherType = Attacher::AttachEngine3D
  Height = 1.5
  Radius = 0.9
FEATURE [Part::Cylinder] Cylinder261
  Angle = 360
  AttacherType = Attacher::AttachEngine3D
  Height = 1.5
  Radius = 0.9
FEATURE [Part::Cylinder] Cylinder262
  Angle = 360
  AttacherType = Attacher::AttachEngine3D
  Height = 1.5
  Radius = 0.9
FEATURE [Part::Cut] Cut159
  Base = -> Cylinder262
  Placement = pos=(22.86,0,0) rot=(0,0,1;0rad)
  Tool = -> Cylinder258
FEATURE [Part::Cylinder] Cylinder263
  Angle = 360
  AttacherType = Attacher::AttachEngine3D
  Height = 1.5
  Radius = 0.4
FEATURE [Part::Cylinder] Cylinder264
  Angle = 360
  AttacherType = Attacher::AttachEngine3D
  Height = 1.5
  Radius = 0.4
FEATURE [Part::Cylinder] Cylinder265
  Angle = 360
  AttacherType = Attacher::AttachEngine3D
  Height = 1.5
  Radius = 0.9
FEATURE [Part::Cylinder] Cylinder266
  Angle = 360
  AttacherType = Attacher::AttachEngine3D
  Height = 1.5
  Radius = 0.9
FEATURE [Part::Cylinder] Cylinder267
  Angle = 360
  AttacherType = Attacher::AttachEngine3D
  Height = 1.5
  Radius = 0.4
FEATURE [Part::Cut] Cut149
  Base = -> Cylinder261
  Placement = pos=(15.24,0,0) rot=(0,0,1;0rad)
  Tool = -> Cylinder267
FEATURE [Part::Cylinder] Cylinder268
  Angle = 360
  AttacherType = Attacher::AttachEngine3D
  Height = 1.5
  Radius = 0.9
FEATURE [Part::Cylinder] Cylinder269
  Angle = 360
  AttacherType = Attacher::AttachEngine3D
  Height = 1.5
  Radius = 0.4
FEATURE [Part::Cut] Cut150
  Base = -> Cylinder268
  Placement = pos=(2.54,0,0) rot=(0,0,1;0rad)
  Tool = -> Cylinder269
FEATURE [Part::Cylinder] Cylinder270
  Angle = 360
  AttacherType = Attacher::AttachEngine3D
  Height = 1.5
  Radius = 0.4
FEATURE [Part::Cut] Cut162
  Base = -> Cylinder265
  Placement = pos=(20.32,0,0) rot=(0,0,1;0rad)
  Tool = -> Cylinder270
FEATURE [Part::Cylinder] Cylinder271
  Angle = 360
  AttacherType = Attacher::AttachEngine3D
  Height = 1.5
  Radius = 0.4
FEATURE [Part::Cut] Cut156
  Base = -> Cylinder266
  Placement = pos=(5.08,0,0) rot=(0,0,1;0rad)
  Tool = -> Cylinder271
FEATURE [Part::Cylinder] Cylinder272
  Angle = 360
  AttacherType = Attacher::AttachEngine3D
  Height = 1.5
  Radius = 0.4
FEATURE [Part::Cylinder] Cylinder273
  Angle = 360
  AttacherType = Attacher::AttachEngine3D
  Height = 1.5
  Radius = 0.4
FEATURE [Part::Cylinder] Cylinder274
  Angle = 360
  AttacherType = Attacher::AttachEngine3D
  Height = 1.5
  Radius = 0.9
FEATURE [Part::Cut] Cut161
  Base = -> Cylinder274
  Placement = pos=(10.16,0,0) rot=(0,0,1;0rad)
  Tool = -> Cylinder272
FEATURE [Part::Cylinder] Cylinder275
  Angle = 360
  AttacherType = Attacher::AttachEngine3D
  Height = 1.5
  Radius = 0.9
FEATURE [Part::Cut] Cut148
  Base = -> Cylinder275
  Placement = pos=(7.62,0,0) rot=(0,0,1;0rad)
  Tool = -> Cylinder257
FEATURE [Part::Cylinder] Cylinder276
  Angle = 360
  AttacherType = Attacher::AttachEngine3D
  Height = 1.5
  Radius = 0.9
FEATURE [Part::Cylinder] Cylinder277
  Angle = 360
  AttacherType = Attacher::AttachEngine3D
  Height = 1.5
  Radius = 0.4
FEATURE [Part::Cut] Cut155
  Base = -> Cylinder276
  Placement = pos=(17.78,0,0) rot=(0,0,1;0rad)
  Tool = -> Cylinder277
FEATURE [Part::Cylinder] Cylinder278
  Angle = 360
  AttacherType = Attacher::AttachEngine3D
  Height = 1.5
  Radius = 0.9
FEATURE [Part::Cut] Cut157
  Base = -> Cylinder278
  Placement = pos=(12.7,0,0) rot=(0,0,1;0rad)
  Tool = -> Cylinder263
FEATURE [Part::Cylinder] Cylinder279
  Angle = 360
  AttacherType = Attacher::AttachEngine3D
  Height = 1.5
  Radius = 0.9
FEATURE [Part::Cylinder] Cylinder280
  Angle = 360
  AttacherType = Attacher::AttachEngine3D
  Height = 1.5
  Radius = 0.4
FEATURE [Part::Cylinder] Cylinder281
  Angle = 360
  AttacherType = Attacher::AttachEngine3D
  Height = 1.5
  Radius = 0.4
FEATURE [Part::Cylinder] Cylinder282
  Angle = 360
  AttacherType = Attacher::AttachEngine3D
  Height = 1.5
  Radius = 0.9
FEATURE [Part::Cylinder] Cylinder283 .. Cylinder288  x6 (patterned run collapsed; names and placements below)
  Angle = 360
  AttacherType = Attacher::AttachEngine3D
  Height = 1.5
  Radius = 0.4
FEATURE [Part::Cylinder] Cylinder289
  Angle = 360
  AttacherType = Attacher::AttachEngine3D
  Height = 1.5
  Radius = 0.9
FEATURE [Part::Cylinder] Cylinder290
  Angle = 360
  AttacherType = Attacher::AttachEngine3D
  Height = 1.5
  Radius = 0.9
FEATURE [Part::Cut] Cut154
  Base = -> Cylinder290
  Placement = pos=(17.78,0,0) rot=(0,0,1;0rad)
  Tool = -> Cylinder264
FEATURE [Part::Cylinder] Cylinder291
  Angle = 360
  AttacherType = Attacher::AttachEngine3D
  Height = 1.5
  Radius = 0.4
FEATURE [Part::Cylinder] Cylinder292
  Angle = 360
  AttacherType = Attacher::AttachEngine3D
  Height = 1.5
  Radius = 0.9
FEATURE [Part::Cylinder] Cylinder293
  Angle = 360
  AttacherType = Attacher::AttachEngine3D
  Height = 1.5
  Radius = 0.4
FEATURE [Part::Cylinder] Cylinder294
  Angle = 360
  AttacherType = Attacher::AttachEngine3D
  Height = 1.5
  Radius = 0.9
FEATURE [Part::Cut] Cut152
  Base = -> Cylinder294
  Placement = pos=(7.62,0,0) rot=(0,0,1;0rad)
  Tool = -> Cylinder280
FEATURE [Part::Cylinder] Cylinder295
  Angle = 360
  AttacherType = Attacher::AttachEngine3D
  Height = 1.5
  Radius = 0.4
FEATURE [Part::Cylinder] Cylinder296
  Angle = 360
  AttacherType = Attacher::AttachEngine3D
  Height = 1.5
  Radius = 0.4
FEATURE [Part::Cut] Cut151
  Base = -> Cylinder260
  Placement = pos=(15.24,0,0) rot=(0,0,1;0rad)
  Tool = -> Cylinder296
FEATURE [Part::Box] Box233  label="Cube211"
  AttacherType = Attacher::AttachEngine3D
  Height = 1.5
  Length = 1.8
  Placement = pos=(-0.9,-0.9,0) rot=(0,0,1;0rad)
  Width = 1.8
FEATURE [Part::Cylinder] Cylinder297
  Angle = 360
  AttacherType = Attacher::AttachEngine3D
  Height = 1.5
  Radius = 0.4
FEATURE [Part::Cylinder] Cylinder298
  Angle = 360
  AttacherType = Attacher::AttachEngine3D
  Height = 1.5
  Radius = 0.9
FEATURE [Part::Cut] Cut153
  Base = -> Cylinder298
  Placement = pos=(5.08,0,0) rot=(0,0,1;0rad)
  Tool = -> Cylinder288
FEATURE [Part::Cylinder] Cylinder299
  Angle = 360
  AttacherType = Attacher::AttachEngine3D
  Height = 1.5
  Radius = 0.4
FEATURE [Part::Cylinder] Cylinder300
  Angle = 360
  AttacherType = Attacher::AttachEngine3D
  Height = 1.5
  Radius = 0.9
FEATURE [Part::Cylinder] Cylinder301
  Angle = 360
  AttacherType = Attacher::AttachEngine3D
  Height = 1.5
  Radius = 0.4
FEATURE [Part::Cylinder] Cylinder302
  Angle = 360
  AttacherType = Attacher::AttachEngine3D
  Height = 1.5
  Radius = 0.9
FEATURE [Part::Cylinder] Cylinder303
  Angle = 360
  AttacherType = Attacher::AttachEngine3D
  Height = 1.5
  Radius = 0.9
FEATURE [Mesh::Feature] __54_pin_header011  label="2.54_pin_header011"
  Placement = pos=(21.2,27.2,-0.8) rot=(0,0,1;0rad)
FEATURE [Part::Cut] Cut163
  Base = -> Cylinder282
  Placement = pos=(17.78,0,0) rot=(0,0,1;0rad)
  Tool = -> Cylinder287
FEATURE [Part::Cut] Cut167
  Base = -> Cylinder302
  Placement = pos=(7.62,0,0) rot=(0,0,1;0rad)
  Tool = -> Cylinder299
FEATURE [Part::Cut] Cut169
  Base = -> Cylinder289
  Placement = pos=(10.16,0,0) rot=(0,0,1;0rad)
  Tool = -> Cylinder291
FEATURE [Part::Cut] Cut170
  Base = -> Cylinder254
  Placement = pos=(22.86,0,0) rot=(0,0,1;0rad)
  Tool = -> Cylinder259
FEATURE [Part::Cut] Cut171
  Base = -> Cylinder279
  Placement = pos=(12.7,0,0) rot=(0,0,1;0rad)
  Tool = -> Cylinder284
FEATURE [Part::Cut] Cut172
  Base = -> Cylinder303
  Placement = pos=(2.54,0,0) rot=(0,0,1;0rad)
  Tool = -> Cylinder295
FEATURE [Part::Cut] Cut175
  Base = -> Cylinder292
  Placement = pos=(5.08,0,0) rot=(0,0,1;0rad)
  Tool = -> Cylinder301
FEATURE [Part::Cut] Cut176
  Base = -> Cylinder300
  Placement = pos=(20.32,0,0) rot=(0,0,1;0rad)
  Tool = -> Cylinder293
FEATURE [Part::Compound] Compound132  label="contact row 008"
  Links = -> [Cut170,Cut158,Cut154,Cut151,Cut152,Cut153,Cut172,Cut169,Cut176,Cut171]
  Placement = pos=(8.5,1.73,0) rot=(0,0,1;0rad)
FEATURE [Part::Cut] Cut182
  Base = -> Box233
  Tool = -> Cylinder273
FEATURE [Part::Compound] Compound126  label="contact row 005"
  Links = -> [Cut182,Cut159,Cut155,Cut149,Cut148,Cut156,Cut150,Cut161,Cut157,Cut162]
  Placement = pos=(8.5,4.27,0) rot=(0,0,1;0rad)
FEATURE [Part::Cylinder] Cylinder304
  Angle = 360
  AttacherType = Attacher::AttachEngine3D
  Height = 1.5
  Radius = 0.4
FEATURE [Part::Cylinder] Cylinder305
  Angle = 360
  AttacherType = Attacher::AttachEngine3D
  Height = 1.5
  Radius = 0.4
FEATURE [Part::Cylinder] Cylinder306
  Angle = 360
  AttacherType = Attacher::AttachEngine3D
  Height = 1.5
  Radius = 0.9
FEATURE [Part::Cut] Cut179
  Base = -> Cylinder306
  Placement = pos=(12.7,0,0) rot=(0,0,1;0rad)
  Tool = -> Cylinder283
FEATURE [Part::Cylinder] Cylinder307
  Angle = 360
  AttacherType = Attacher::AttachEngine3D
  Height = 1.5
  Radius = 0.4
FEATURE [Part::Cylinder] Cylinder308
  Angle = 360
  AttacherType = Attacher::AttachEngine3D
  Height = 1.5
  Radius = 0.9
FEATURE [Part::Cut] Cut180
  Base = -> Cylinder308
  Placement = pos=(10.16,0,0) rot=(0,0,1;0rad)
  Tool = -> Cylinder285
FEATURE [Part::Cylinder] Cylinder309
  Angle = 360
  AttacherType = Attacher::AttachEngine3D
  Height = 1.5
  Radius = 0.9
FEATURE [Part::Cylinder] Cylinder310
  Angle = 360
  AttacherType = Attacher::AttachEngine3D
  Height = 1.5
  Placement = pos=(12.7,0,0) rot=(0,0,1;0rad)
  Radius = 0.9
FEATURE [Part::Cylinder] Cylinder311
  Angle = 360
  AttacherType = Attacher::AttachEngine3D
  Height = 1.5
  Placement = pos=(2.54,0,0) rot=(0,0,1;0rad)
  Radius = 0.9
FEATURE [Part::Cylinder] Cylinder312
  Angle = 360
  AttacherType = Attacher::AttachEngine3D
  Height = 1.5
  Radius = 0.9
FEATURE [Part::Cut] Cut174
  Base = -> Cylinder312
  Placement = pos=(2.54,0,0) rot=(0,0,1;0rad)
  Tool = -> Cylinder297
FEATURE [Part::Cylinder] Cylinder313
  Angle = 360
  AttacherType = Attacher::AttachEngine3D
  Height = 1.5
  Radius = 0.9
FEATURE [Part::Cut] Cut181
  Base = -> Cylinder313
  Placement = pos=(15.24,0,0) rot=(0,0,1;0rad)
  Tool = -> Cylinder281
FEATURE [Part::Cylinder] Cylinder314
  Angle = 360
  AttacherType = Attacher::AttachEngine3D
  Height = 1.5
  Radius = 0.9
FEATURE [Part::Cut] Cut173
  Base = -> Cylinder314
  Placement = pos=(20.32,0,0) rot=(0,0,1;0rad)
  Tool = -> Cylinder286
FEATURE [Part::Cylinder] Cylinder315
  Angle = 360
  AttacherType = Attacher::AttachEngine3D
  Height = 1.5
  Radius = 0.9
FEATURE [Part::Cylinder] Cylinder316
  Angle = 360
  AttacherType = Attacher::AttachEngine3D
  Height = 1.5
  Radius = 0.4
FEATURE [Part::Cylinder] Cylinder317
  Angle = 360
  AttacherType = Attacher::AttachEngine3D
  Height = 1.5
  Radius = 0.9
FEATURE [Part::Cylinder] Cylinder318
  Angle = 360
  AttacherType = Attacher::AttachEngine3D
  Height = 1.5
  Radius = 0.9
FEATURE [Part::Cylinder] Cylinder319
  Angle = 360
  AttacherType = Attacher::AttachEngine3D
  Height = 1.5
  Radius = 0.9
FEATURE [Part::Cylinder] Cylinder320
  Angle = 360
  AttacherType = Attacher::AttachEngine3D
  Height = 1.5
  Radius = 0.4
FEATURE [Part::Cut] Cut164
  Base = -> Cylinder318
  Tool = -> Cylinder320
FEATURE [Part::Box] Box234  label="Cube212"
  AttacherType = Attacher::AttachEngine3D
  Height = 1.5
  Length = 1.8
  Placement = pos=(-0.9,-0.9,0) rot=(0,0,1;0rad)
  Width = 1.8
FEATURE [Part::Cylinder] Cylinder321
  Angle = 360
  AttacherType = Attacher::AttachEngine3D
  Height = 1.5
  Radius = 0.9
FEATURE [Part::Cylinder] Cylinder322
  Angle = 360
  AttacherType = Attacher::AttachEngine3D
  Height = 1.5
  Radius = 0.4
FEATURE [Part::Cut] Cut165
  Base = -> Cylinder309
  Placement = pos=(20.32,0,0) rot=(0,0,1;0rad)
  Tool = -> Cylinder322
FEATURE [Part::Cylinder] Cylinder323
  Angle = 360
  AttacherType = Attacher::AttachEngine3D
  Height = 1.5
  Radius = 0.9
FEATURE [Part::Cut] Cut177
  Base = -> Cylinder323
  Placement = pos=(15.24,0,0) rot=(0,0,1;0rad)
  Tool = -> Cylinder305
FEATURE [Part::Cylinder] Cylinder324
  Angle = 360
  AttacherType = Attacher::AttachEngine3D
  Height = 1.5
  Radius = 0.4
FEATURE [Part::Cut] Cut178
  Base = -> Cylinder319
  Placement = pos=(7.62,0,0) rot=(0,0,1;0rad)
  Tool = -> Cylinder324
FEATURE [Part::Cylinder] Cylinder325
  Angle = 360
  AttacherType = Attacher::AttachEngine3D
  Height = 1.5
  Radius = 0.4
FEATURE [Part::Cylinder] Cylinder326
  Angle = 360
  AttacherType = Attacher::AttachEngine3D
  Height = 1.5
  Radius = 0.4
FEATURE [Part::Cut] Cut166
  Base = -> Cylinder315
  Placement = pos=(22.86,0,0) rot=(0,0,1;0rad)
  Tool = -> Cylinder326
FEATURE [Part::Compound] Compound127  label="contact row 006"
  Links = -> [Cut166,Cut164,Cut163,Cut181,Cut167,Cut175,Cut174,Cut180,Cut173,Cut179]
  Placement = pos=(8.5,27.13,0) rot=(0,0,1;0rad)
FEATURE [Part::Cylinder] Cylinder327
  Angle = 360
  AttacherType = Attacher::AttachEngine3D
  Height = 1.5
  Radius = 0.4
FEATURE [Part::Cylinder] Cylinder328
  Angle = 360
  AttacherType = Attacher::AttachEngine3D
  Height = 1.5
  Radius = 0.9
FEATURE [Part::Cylinder] Cylinder329
  Angle = 360
  AttacherType = Attacher::AttachEngine3D
  Height = 1.5
  Radius = 0.9
FEATURE [Part::Cylinder] Cylinder330
  Angle = 360
  AttacherType = Attacher::AttachEngine3D
  Height = 1.5
  Radius = 0.4
FEATURE [Part::Cylinder] Cylinder331
  Angle = 360
  AttacherType = Attacher::AttachEngine3D
  Height = 1.5
  Radius = 0.9
FEATURE [Part::Cut] Cut168
  Base = -> Cylinder331
  Placement = pos=(17.78,0,0) rot=(0,0,1;0rad)
  Tool = -> Cylinder325
FEATURE [Part::Cylinder] Cylinder332
  Angle = 360
  AttacherType = Attacher::AttachEngine3D
  Height = 1.5
  Radius = 0.4
FEATURE [Part::Cylinder] Cylinder333
  Angle = 360
  AttacherType = Attacher::AttachEngine3D
  Height = 1.5
  Radius = 0.9
FEATURE [Part::Cylinder] Cylinder334
  Angle = 360
  AttacherType = Attacher::AttachEngine3D
  Height = 1.5
  Placement = pos=(5.08,0,0) rot=(0,0,1;0rad)
  Radius = 0.9
FEATURE [Part::Cylinder] Cylinder335
  Angle = 360
  AttacherType = Attacher::AttachEngine3D
  Height = 1.5
  Placement = pos=(10.16,0,0) rot=(0,0,1;0rad)
  Radius = 0.9
FEATURE [Part::Cylinder] Cylinder336
  Angle = 360
  AttacherType = Attacher::AttachEngine3D
  Height = 1.5
  Placement = pos=(5.08,0,0) rot=(0,0,1;0rad)
  Radius = 0.9
FEATURE [Part::Cylinder] Cylinder337
  Angle = 360
  AttacherType = Attacher::AttachEngine3D
  Height = 1.5
  Placement = pos=(12.7,0,0) rot=(0,0,1;0rad)
  Radius = 0.9
FEATURE [Part::Cylinder] Cylinder338
  Angle = 360
  AttacherType = Attacher::AttachEngine3D
  Height = 1.5
  Placement = pos=(2.54,0,0) rot=(0,0,1;0rad)
  Radius = 0.9
FEATURE [Part::Cylinder] Cylinder339
  Angle = 360
  AttacherType = Attacher::AttachEngine3D
  Height = 1.5
  Placement = pos=(15.24,0,0) rot=(0,0,1;0rad)
  Radius = 0.9
FEATURE [Part::Cylinder] Cylinder340
  Angle = 360
  AttacherType = Attacher::AttachEngine3D
  Height = 1.5
  Placement = pos=(22.86,0,0) rot=(0,0,1;0rad)
  Radius = 0.9
FEATURE [Part::Cylinder] Cylinder341
  Angle = 360
  AttacherType = Attacher::AttachEngine3D
  Height = 1.5
  Placement = pos=(7.62,0,0) rot=(0,0,1;0rad)
  Radius = 0.9
FEATURE [Part::Cylinder] Cylinder342
  Angle = 360
  AttacherType = Attacher::AttachEngine3D
  Height = 1.5
  Radius = 0.9
FEATURE [Part::Cylinder] Cylinder343
  Angle = 360
  AttacherType = Attacher::AttachEngine3D
  Height = 1.5
  Placement = pos=(22.86,0,0) rot=(0,0,1;0rad)
  Radius = 0.9
FEATURE [Part::Cylinder] Cylinder344
  Angle = 360
  AttacherType = Attacher::AttachEngine3D
  Height = 1.5
  Placement = pos=(15.24,0,0) rot=(0,0,1;0rad)
  Radius = 0.9
FEATURE [Part::Cylinder] Cylinder345
  Angle = 360
  AttacherType = Attacher::AttachEngine3D
  Height = 1.5
  Placement = pos=(7.62,0,0) rot=(0,0,1;0rad)
  Radius = 0.9
FEATURE [Part::Cylinder] Cylinder346
  Angle = 360
  AttacherType = Attacher::AttachEngine3D
  Height = 1.5
  Placement = pos=(10.16,0,0) rot=(0,0,1;0rad)
  Radius = 0.9
FEATURE [Part::Box] Box235  label="Cube213"
  AttacherType = Attacher::AttachEngine3D
  Height = 1.5
  Length = 1.8
  Placement = pos=(-0.9,-0.9,0) rot=(0,0,1;0rad)
  Width = 1.8
FEATURE [Part::Cylinder] Cylinder347
  Angle = 360
  AttacherType = Attacher::AttachEngine3D
  Height = 1.5
  Placement = pos=(20.32,0,0) rot=(0,0,1;0rad)
  Radius = 0.9
FEATURE [Part::Cylinder] Cylinder348
  Angle = 360
  AttacherType = Attacher::AttachEngine3D
  Height = 1.5
  Placement = pos=(5.08,0,0) rot=(0,0,1;0rad)
  Radius = 0.9
FEATURE [Part::Cylinder] Cylinder349
  Angle = 360
  AttacherType = Attacher::AttachEngine3D
  Height = 1.5
  Placement = pos=(12.7,0,0) rot=(0,0,1;0rad)
  Radius = 0.9
FEATURE [Part::Cylinder] Cylinder350
  Angle = 360
  AttacherType = Attacher::AttachEngine3D
  Height = 1.5
  Placement = pos=(10.16,0,0) rot=(0,0,1;0rad)
  Radius = 0.9
FEATURE [Part::Cylinder] Cylinder351
  Angle = 360
  AttacherType = Attacher::AttachEngine3D
  Height = 1.5
  Placement = pos=(2.54,0,0) rot=(0,0,1;0rad)
  Radius = 0.9
FEATURE [Part::Cylinder] Cylinder352
  Angle = 360
  AttacherType = Attacher::AttachEngine3D
  Height = 1.5
  Placement = pos=(17.78,0,0) rot=(0,0,1;0rad)
  Radius = 0.9
FEATURE [Part::Compound] Compound130  label="Compound157"
  Links = -> [Cylinder342,Cylinder336,Cylinder337,Cylinder346,Cylinder338,Cylinder341,Cylinder343,Cylinder344,Cylinder352,Cylinder347]
  Placement = pos=(8.5,1.73,0) rot=(0,0,1;0rad)
FEATURE [Part::Cylinder] Cylinder353
  Angle = 360
  AttacherType = Attacher::AttachEngine3D
  Height = 1.5
  Placement = pos=(17.78,0,0) rot=(0,0,1;0rad)
  Radius = 0.9
FEATURE [Part::Cylinder] Cylinder354
  Angle = 360
  AttacherType = Attacher::AttachEngine3D
  Height = 1.5
  Placement = pos=(20.32,0,0) rot=(0,0,1;0rad)
  Radius = 0.9
FEATURE [Part::Compound] Compound129
  Links = -> [Cylinder340,Cylinder334,Cylinder310,Cylinder335,Cylinder311,Cylinder345,Cylinder339,Cylinder353,Cylinder354,Box235]
  Placement = pos=(8.5,4.27,0) rot=(0,0,1;0rad)
FEATURE [Part::Cut] Cut187
  Base = -> Cylinder317
  Placement = pos=(5.08,0,0) rot=(0,0,1;0rad)
  Tool = -> Cylinder327
FEATURE [Part::Cut] Cut189
  Base = -> Box234
  Tool = -> Cylinder307
FEATURE [Part::Cut] Cut190
  Base = -> Cylinder321
  Placement = pos=(22.86,0,0) rot=(0,0,1;0rad)
  Tool = -> Cylinder304
FEATURE [Part::Cut] Cut192
  Base = -> Cylinder328
  Placement = pos=(2.54,0,0) rot=(0,0,1;0rad)
  Tool = -> Cylinder316
FEATURE [Part::Cut] Cut195
  Base = -> Cylinder329
  Placement = pos=(10.16,0,0) rot=(0,0,1;0rad)
  Tool = -> Cylinder332
FEATURE [Part::Cut] Cut196
  Base = -> Cylinder333
  Placement = pos=(12.7,0,0) rot=(0,0,1;0rad)
  Tool = -> Cylinder330
FEATURE [Part::Compound] Compound128  label="contact row 007"
  Links = -> [Cut189,Cut165,Cut168,Cut177,Cut178,Cut187,Cut192,Cut195,Cut196,Cut190]
  Placement = pos=(8.5,29.67,0) rot=(0,0,1;0rad)
FEATURE [Part::Cylinder] Cylinder355
  Angle = 360
  AttacherType = Attacher::AttachEngine3D
  Height = 1.5
  Placement = pos=(20.32,0,0) rot=(0,0,1;0rad)
  Radius = 0.9
FEATURE [Part::Cylinder] Cylinder356
  Angle = 360
  AttacherType = Attacher::AttachEngine3D
  Height = 1.5
  Placement = pos=(10.16,0,0) rot=(0,0,1;0rad)
  Radius = 0.9
FEATURE [Part::Cylinder] Cylinder357
  Angle = 360
  AttacherType = Attacher::AttachEngine3D
  Height = 1.3
  Placement = pos=(-7,1.3,-17) rot=(1,0,0;1.5708rad)
  Radius = 0.9
FEATURE [Part::Box] Box236  label="Cube214"
  AttacherType = Attacher::AttachEngine3D
  Height = 36.5
  Length = 24.5
  Placement = pos=(-24.5,0,-19.5) rot=(0,0,1;0rad)
  Width = 1.3
FEATURE [Part::Cylinder] Cylinder358
  Angle = 360
  AttacherType = Attacher::AttachEngine3D
  Height = 10
  Placement = pos=(-14.5,2,14) rot=(1,0,0;1.5708rad)
  Radius = 2
FEATURE [Part::Cylinder] Cylinder359
  Angle = 360
  AttacherType = Attacher::AttachEngine3D
  Height = 1.3
  Placement = pos=(-9.54,1.3,-17) rot=(1,0,0;1.5708rad)
  Radius = 0.9
FEATURE [Part::Cylinder] Cylinder360
  Angle = 360
  AttacherType = Attacher::AttachEngine3D
  Height = 10
  Placement = pos=(-21.5,2,-16.5) rot=(1,0,0;1.5708rad)
  Radius = 2
FEATURE [Part::Cylinder] Cylinder361
  Angle = 360
  AttacherType = Attacher::AttachEngine3D
  Height = 1.5
  Radius = 0.9
FEATURE [Part::Cylinder] Cylinder362
  Angle = 360
  AttacherType = Attacher::AttachEngine3D
  Height = 1.5
  Placement = pos=(17.78,0,0) rot=(0,0,1;0rad)
  Radius = 0.9
FEATURE [Part::Cylinder] Cylinder363
  Angle = 360
  AttacherType = Attacher::AttachEngine3D
  Height = 1.3
  Radius = 0.9
FEATURE [Part::Cylinder] Cylinder364
  Angle = 360
  AttacherType = Attacher::AttachEngine3D
  Height = 1.3
  Placement = pos=(-12.08,1.3,-17) rot=(1,0,0;1.5708rad)
  Radius = 0.9
FEATURE [Part::Cylinder] Cylinder365
  Angle = 360
  AttacherType = Attacher::AttachEngine3D
  Height = 1.3
  Radius = 0.4
FEATURE [Part::Cylinder] Cylinder366
  Angle = 360
  AttacherType = Attacher::AttachEngine3D
  Height = 1.5
  Placement = pos=(5.08,0,0) rot=(0,0,1;0rad)
  Radius = 0.9
FEATURE [Part::Box] Box237  label="Cube215"
  AttacherType = Attacher::AttachEngine3D
  Height = 1.5
  Length = 1.8
  Placement = pos=(-0.9,-0.9,0) rot=(0,0,1;0rad)
  Width = 1.8
FEATURE [Part::Cylinder] Cylinder367
  Angle = 360
  AttacherType = Attacher::AttachEngine3D
  Height = 1.3
  Radius = 0.4
FEATURE [Part::Cylinder] Cylinder368
  Angle = 360
  AttacherType = Attacher::AttachEngine3D
  Height = 1.3
  Placement = pos=(-14.62,1.3,-17) rot=(1,0,0;1.5708rad)
  Radius = 0.9
FEATURE [Part::Cylinder] Cylinder369
  Angle = 360
  AttacherType = Attacher::AttachEngine3D
  Height = 1.3
  Radius = 0.9
FEATURE [Part::Cylinder] Cylinder370
  Angle = 360
  AttacherType = Attacher::AttachEngine3D
  Height = 1.5
  Placement = pos=(7.62,0,0) rot=(0,0,1;0rad)
  Radius = 0.9
FEATURE [Part::Cylinder] Cylinder371
  Angle = 360
  AttacherType = Attacher::AttachEngine3D
  Height = 1.5
  Placement = pos=(15.24,0,0) rot=(0,0,1;0rad)
  Radius = 0.9
FEATURE [Part::Cylinder] Cylinder372
  Angle = 360
  AttacherType = Attacher::AttachEngine3D
  Height = 1.5
  Placement = pos=(22.86,0,0) rot=(0,0,1;0rad)
  Radius = 0.9
FEATURE [Part::Cylinder] Cylinder373
  Angle = 360
  AttacherType = Attacher::AttachEngine3D
  Height = 1.5
  Placement = pos=(12.7,0,0) rot=(0,0,1;0rad)
  Radius = 0.9
FEATURE [Part::Cylinder] Cylinder374
  Angle = 360
  AttacherType = Attacher::AttachEngine3D
  Height = 1.5
  Placement = pos=(15.24,0,0) rot=(0,0,1;0rad)
  Radius = 0.9
FEATURE [Part::Cylinder] Cylinder375
  Angle = 360
  AttacherType = Attacher::AttachEngine3D
  Height = 1.5
  Placement = pos=(17.78,0,0) rot=(0,0,1;0rad)
  Radius = 0.9
FEATURE [Part::Cylinder] Cylinder376
  Angle = 360
  AttacherType = Attacher::AttachEngine3D
  Height = 1.5
  Placement = pos=(20.32,0,0) rot=(0,0,1;0rad)
  Radius = 0.9
FEATURE [Part::Cylinder] Cylinder377
  Angle = 360
  AttacherType = Attacher::AttachEngine3D
  Height = 1.3
  Radius = 0.9
FEATURE [Part::Cut] Cut193  label="contact011"
  Base = -> Cylinder377
  Placement = pos=(-7,1.3,-17) rot=(1,0,0;1.5708rad)
  Tool = -> Cylinder367
FEATURE [Part::Cylinder] Cylinder378
  Angle = 360
  AttacherType = Attacher::AttachEngine3D
  Height = 1.5
  Placement = pos=(22.86,0,0) rot=(0,0,1;0rad)
  Radius = 0.9
FEATURE [Part::Compound] Compound151  label="Compound156"
  Links = -> [Cylinder361,Cylinder348,Cylinder349,Cylinder350,Cylinder351,Cylinder370,Cylinder378,Cylinder371,Cylinder362,Cylinder355]
  Placement = pos=(8.5,27.13,0) rot=(0,0,1;0rad)
FEATURE [Part::Cylinder] Cylinder379
  Angle = 360
  AttacherType = Attacher::AttachEngine3D
  Height = 1.5
  Placement = pos=(2.54,0,0) rot=(0,0,1;0rad)
  Radius = 0.9
FEATURE [Part::Cylinder] Cylinder380
  Angle = 360
  AttacherType = Attacher::AttachEngine3D
  Height = 1.5
  Placement = pos=(7.62,0,0) rot=(0,0,1;0rad)
  Radius = 0.9
FEATURE [Part::Compound] Compound141  label="Compound174"
  Links = -> [Cylinder372,Cylinder366,Cylinder373,Cylinder356,Cylinder379,Cylinder380,Cylinder374,Cylinder375,Cylinder376,Box237]
  Placement = pos=(8.5,29.67,0) rot=(0,0,1;0rad)
FEATURE [Part::MultiFuse] Fusion062
  Shapes = -> [Compound129,Compound141,Compound130,Compound151]
FEATURE [Part::Cut] Cut183  label="PCB with holes001"
  Base = -> Cut160
  Tool = -> Fusion062
FEATURE [Part::Compound] Compound149  label="Compound173"
  Links = -> [Box229,Box230,Box231,__54_pin_header009,_73460003,Box232,Cut183,Compound132,Compound126,__54_pin_header010,Compound127,__54_pin_header008,__54_pin_header011,Compound128]
  Placement = pos=(0,0,0) rot=(0,1,0;1.5708rad)
FEATURE [Part::MultiFuse] Fusion063  label="ESP32 mini kit001"
  Placement = pos=(68.5,42.5,44.1) rot=(0,0,1;1.5708rad)
  Shapes = -> [Compound149]
FEATURE [Part::Cylinder] Cylinder381
  Angle = 360
  AttacherType = Attacher::AttachEngine3D
  Height = 1.3
  Placement = pos=(-17.16,1.3,-17) rot=(1,0,0;1.5708rad)
  Radius = 0.9
FEATURE [Part::MultiFuse] Fusion064
  Shapes = -> [Cylinder357,Cylinder368,Cylinder364,Cylinder381,Cylinder359]
FEATURE [Part::Cylinder] Cylinder382
  Angle = 360
  AttacherType = Attacher::AttachEngine3D
  Height = 10
  Placement = pos=(-3,2,14) rot=(1,0,0;1.5708rad)
  Radius = 2
FEATURE [Part::Cylinder] Cylinder383
  Angle = 360
  AttacherType = Attacher::AttachEngine3D
  Height = 10
  Placement = pos=(-21.5,2,14) rot=(1,0,0;1.5708rad)
  Radius = 2
FEATURE [Part::Cylinder] Cylinder384
  Angle = 360
  AttacherType = Attacher::AttachEngine3D
  Height = 10
  Placement = pos=(-3,2,-16.5) rot=(1,0,0;1.5708rad)
  Radius = 2
FEATURE [Part::Box] Box238  label="Cube216"
  AttacherType = Attacher::AttachEngine3D
  Height = 12
  Length = 16
  Placement = pos=(-18,1.3,-6) rot=(0,0,1;0rad)
  Width = 3
FEATURE [Part::Fillet] Fillet030  label="neo6m chip001"
  Base = -> Box238
  Edges = 4 edges r=0.5: [Edge3,Edge7,Edge11,Edge12]
FEATURE [Part::Cylinder] Cylinder385
  Angle = 360
  AttacherType = Attacher::AttachEngine3D
  Height = 1.3
  Radius = 0.4
FEATURE [Part::Cut] Cut184  label="contact006"
  Base = -> Cylinder369
  Placement = pos=(-9.54,1.3,-17) rot=(1,0,0;1.5708rad)
  Tool = -> Cylinder385
FEATURE [Part::Cylinder] Cylinder386
  Angle = 360
  AttacherType = Attacher::AttachEngine3D
  Height = 1.3
  Radius = 0.4
FEATURE [Part::Cut] Cut186  label="contact008"
  Base = -> Cylinder363
  Placement = pos=(-12.08,1.3,-17) rot=(1,0,0;1.5708rad)
  Tool = -> Cylinder386
FEATURE [Part::Cylinder] Cylinder387
  Angle = 360
  AttacherType = Attacher::AttachEngine3D
  Height = 1.3
  Radius = 0.4
FEATURE [Part::Cylinder] Cylinder388
  Angle = 360
  AttacherType = Attacher::AttachEngine3D
  Height = 1.3
  Radius = 0.9
FEATURE [Part::Cut] Cut185  label="contact007"
  Base = -> Cylinder388
  Placement = pos=(-14.62,1.3,-17) rot=(1,0,0;1.5708rad)
  Tool = -> Cylinder387
FEATURE [Part::Cylinder] Cylinder389
  Angle = 360
  AttacherType = Attacher::AttachEngine3D
  Height = 1.3
  Radius = 0.4
FEATURE [Part::Cylinder] Cylinder390
  Angle = 360
  AttacherType = Attacher::AttachEngine3D
  Height = 1.3
  Radius = 0.9
FEATURE [Part::Cut] Cut191  label="contact010"
  Base = -> Cylinder390
  Placement = pos=(-7,1.3,-17) rot=(1,0,0;1.5708rad)
  Tool = -> Cylinder389
FEATURE [Part::Cylinder] Cylinder391
  Angle = 360
  AttacherType = Attacher::AttachEngine3D
  Height = 1.3
  Radius = 0.9
FEATURE [Part::Cut] Cut188  label="contact009"
  Base = -> Cylinder391
  Placement = pos=(-17.16,1.3,-17) rot=(1,0,0;1.5708rad)
  Tool = -> Cylinder365
FEATURE [Part::MultiFuse] Fusion065  label="pcb cutouts001"
  Shapes = -> [Fusion064,Cylinder382,Cylinder358,Cylinder383,Cylinder384,Cylinder360]
FEATURE [Part::Cut] Cut194  label="PCB006"
  Base = -> Box236
  Tool = -> Fusion065
FEATURE [Part::Feature] Part__Feature437  label="GPS_connector001"
  Placement = pos=(-0.2977,1.3,-0.303869) rot=(-1,0,0;1.5708rad)
  shape: bbox 5.25 x 2.059 x 3.5 mm, 38 faces (baked)
FEATURE [Part::Feature] Part__Feature447  label="Antenna_connector001"
  Placement = pos=(1.97581,1.55,13.0153) rot=(-0.997842,-0.046433,-0.046433;1.57296rad)
  shape: bbox 4.331 x 2.3 x 9.572 mm, 71 faces (baked)
FEATURE [Part::Compound] Compound154  label="meo6mv003"
  Links = -> [Cut191,Cut188,Part__Feature447,Part__Feature430,Part__Feature425,Part__Feature426,Part__Feature424,Part__Feature428,Part__Feature429,Part__Feature437,Fillet030,Part__Feature427,Cut194,Cut193,Cut185,Part__Feature431,Cut186,Cut184]
  Placement = pos=(73.5,44,24.5) rot=(0,0,1;3.14159rad)
FEATURE [Part::Box] Box  label="Cube"
  AttacherType = Attacher::AttachEngine3D
  Height = 45
  Length = 97
  Width = 22
FEATURE [Part::Fillet] Fillet  label="Battery pack"
  Base = -> Box
  Edges = 4 edges r=10.9: [Edge9,Edge10,Edge11,Edge12]
  Placement = pos=(0,0,2.5) rot=(0,0,1;0rad)
FEATURE [Part::Box] Box239  label="USB connector"
  AttacherType = Attacher::AttachEngine3D
  Height = 15
  Length = 15
  Placement = pos=(98,9,8) rot=(0,0,1;0rad)
  Width = 7
FEATURE [Part::Box] Box240  label="Cube218"
  AttacherType = Attacher::AttachEngine3D
  Height = 10
  Length = 155
  Placement = pos=(-10,-10,-10) rot=(0,0,1;0rad)
  Width = 65
FEATURE [Part::Box] Box241  label="Cube219"
  AttacherType = Attacher::AttachEngine3D
  Height = 50
  Length = 155
  Placement = pos=(-10,-10,0) rot=(0,0,1;0rad)
  Width = 10
FEATURE [Part::Box] Box242  label="Cube220"
  AttacherType = Attacher::AttachEngine3D
  Height = 50
  Length = 10
  Placement = pos=(-10,0,0) rot=(0,0,1;0rad)
  Width = 45
FEATURE [Part::Box] Box243  label="Cube221"
  AttacherType = Attacher::AttachEngine3D
  Height = 50
  Length = 10
  Placement = pos=(135,0,0) rot=(0,0,1;0rad)
  Width = 45
FEATURE [Part::Box] Box246  label="ISO lid"
  AttacherType = Attacher::AttachEngine3D
  Height = 10
  Length = 155
  Placement = pos=(-10,-10,50) rot=(0,0,1;0rad)
  Width = 65
FEATURE [Part::Compound] Compound  label="ISO box"
  Links = -> [Box240,Box241,Box243,Box242,Box246]
FEATURE [Part::Box] Box247  label="Baseplate"
  AttacherType = Attacher::AttachEngine3D
  Height = 50
  Length = 135
  Placement = pos=(0,42,0) rot=(0,0,1;0rad)
  Width = 3
FEATURE [Part::Box] Box248  label="cut-out cam large"
  AttacherType = Attacher::AttachEngine3D
  Height = 40.2
  Length = 27.6
  Placement = pos=(5,42,5) rot=(0,0,1;0rad)
  Width = 2
FEATURE [Part::Box] Box249  label="cut-out cam small"
  AttacherType = Attacher::AttachEngine3D
  Height = 32
  Length = 27.6
  Placement = pos=(5,44,10) rot=(0,0,1;0rad)
  Width = 1
FEATURE [Part::Box] Box250  label="cut-out cam sd"
  AttacherType = Attacher::AttachEngine3D
  Height = 8
  Length = 16
  Placement = pos=(11,42,42) rot=(0,0,1;0rad)
  Width = 3
FEATURE [Part::MultiFuse] Fusion  label="Cut-out ESP32CAM"
  Shapes = -> [Box250,Box248,Box249]
FEATURE [Part::Box] Box251  label="Cube224"
  AttacherType = Attacher::AttachEngine3D
  Height = 39.4
  Length = 31.8
  Placement = pos=(37,42,5) rot=(0,0,1;0rad)
  Width = 2
FEATURE [Part::Box] Box252  label="Cube225"
  AttacherType = Attacher::AttachEngine3D
  Height = 37.2
  Length = 29.6
  Placement = pos=(38,44,6) rot=(0,0,1;0rad)
  Width = 1
FEATURE [Part::Box] Box253  label="Cube226"
  AttacherType = Attacher::AttachEngine3D
  Height = 8
  Length = 11
  Placement = pos=(47,42,42) rot=(0,0,1;0rad)
  Width = 3
FEATURE [Part::MultiFuse] Fusion066  label="Cut-out ESP32"
  Shapes = -> [Box253,Box252,Box251]
FEATURE [Part::Box] Box254  label="Cube227"
  AttacherType = Attacher::AttachEngine3D
  Height = 35.9
  Length = 26.8
  Placement = pos=(73,42,5) rot=(0,0,1;0rad)
  Width = 2
FEATURE [Part::Box] Box255  label="Cube228"
  AttacherType = Attacher::AttachEngine3D
  Height = 34.9
  Length = 24.8
  Placement = pos=(74,44,6) rot=(0,0,1;0rad)
  Width = 1
FEATURE [Part::MultiFuse] Fusion067  label="Cut-out NEO6MV2"
  Shapes = -> [Box255,Box254]
FEATURE [Part::Feature] Part__Feature448  label="Antenna004"
  Placement = pos=(133,35,15) rot=(-1,0,0;1.5708rad)
  shape: bbox 6.038 x 7.828 x 16.04 mm, 26 faces (baked)
FEATURE [Part::Box] Box260  label="Cube233"
  AttacherType = Attacher::AttachEngine3D
  Height = 16
  Length = 26.6
  Placement = pos=(102,42,29) rot=(0,0,1;0rad)
  Width = 2
FEATURE [Part::Box] Box261  label="Cube234"
  AttacherType = Attacher::AttachEngine3D
  Height = 13.8
  Length = 24.4
  Placement = pos=(103,44,30) rot=(0,0,1;0rad)
  Width = 1
FEATURE [Part::Box] Box262  label="Cube235"
  AttacherType = Attacher::AttachEngine3D
  Height = 3
  Length = 26.6
  Placement = pos=(102,44,42) rot=(0,0,1;0rad)
  Width = 1
FEATURE [Part::MultiFuse] Fusion070  label="Cut-out MPU9255"
  Placement = pos=(2,0,2) rot=(0,0,1;0rad)
  Shapes = -> [Box260,Box261,Box262]
FEATURE [Part::Box] Box263  label="Cut-out GPS antenna"
  AttacherType = Attacher::AttachEngine3D
  Height = 24.4
  Length = 24.4
  Placement = pos=(105,42,4) rot=(0,0,1;0rad)
  Width = 3
FEATURE [Part::Box] Box264  label="Cube236"
  AttacherType = Attacher::AttachEngine3D
  Height = 10
  Length = 3
  Width = 42
FEATURE [Part::Box] Box265  label="Cube237"
  AttacherType = Attacher::AttachEngine3D
  Height = 10
  Length = 3
  Placement = pos=(0,0,40) rot=(0,0,1;0rad)
  Width = 42
FEATURE [Part::Box] Box266  label="Cube238"
  AttacherType = Attacher::AttachEngine3D
  Height = 50
  Length = 3
  Placement = pos=(0,37,0) rot=(0,0,1;0rad)
  Width = 5
FEATURE [Part::Box] Box268  label="BMP connector"
  AttacherType = Attacher::AttachEngine3D
  Height = 2.5
  Length = 20.7
  Placement = pos=(76,36.5,44) rot=(0,0,1;0rad)
  Width = 8.5
FEATURE [Part::Box] Box269  label="Cube241"
  AttacherType = Attacher::AttachEngine3D
  Height = 2.5
  Length = 20.7
  Placement = pos=(76,47,44) rot=(0,0,1;0rad)
  Width = 8.5
FEATURE [Part::Box] Box270  label="Cut-out header"
  AttacherType = Attacher::AttachEngine3D
  Height = 2.7
  Length = 20.7
  Placement = pos=(76,36.5,44) rot=(0,0,1;0rad)
  Width = 8.9
FEATURE [Part::MultiFuse] Fusion071  label=" Cut-outs"
  Shapes = -> [Fusion070,Fusion,Fusion066,Fusion067,Box263,Box270]
FEATURE [Part::Cut] Cut197  label="Plate"
  Base = -> Box247
  Tool = -> Fusion071
FEATURE [Part::Cone] Cone001
  Angle = 360
  AttacherType = Attacher::AttachEngine3D
  Height = 10
  Placement = pos=(18.5,45,33.5) rot=(-1,0,0;1.5708rad)
  Radius1 = 2
  Radius2 = 5
FEATURE [Part::Box] Box271  label="Cube242"
  AttacherType = Attacher::AttachEngine3D
  Height = 50
  Length = 155
  Placement = pos=(-10,45,0) rot=(1,0,0;0rad)
  Width = 10
FEATURE [Part::Cut] Cut198
  Base = -> Box271
  Tool = -> Cone001
FEATURE [Part::MultiFuse] Fusion072  label="Lid"
  Shapes = -> [Cut198,Box269,Compound021]
FEATURE [Part::Box] Box272  label="Cube243"
  AttacherType = Attacher::AttachEngine3D
  Height = 45
  Length = 97
  Width = 22
FEATURE [Part::Fillet] Fillet031  label="Battery pack001"
  Base = -> Box272
  Edges = 4 edges r=10.9: [Edge9,Edge10,Edge11,Edge12]
  Placement = pos=(0,0,2.5) rot=(0,0,1;0rad)
FEATURE [Part::Box] Box274  label="Cube245"
  AttacherType = Attacher::AttachEngine3D
  Height = 3
  Length = 8
  Placement = pos=(3,32,0) rot=(0,0,1;0rad)
  Width = 8
FEATURE [Part::Chamfer] Chamfer049
  Base = -> Box274
  Edges = 1 edges r=7.9: [Edge5]
  Placement = pos=(0,2,47) rot=(0,0,1;0rad)
FEATURE [Part::Box] Box275  label="Cube246"
  AttacherType = Attacher::AttachEngine3D
  Height = 3
  Length = 8
  Placement = pos=(3,32,0) rot=(0,0,1;0rad)
  Width = 8
FEATURE [Part::Chamfer] Chamfer050
  Base = -> Box275
  Edges = 1 edges r=7.9: [Edge5]
  Placement = pos=(0,2,0) rot=(0,0,1;0rad)
FEATURE [Part::MultiFuse] Fusion073
  Shapes = -> [Chamfer050,Chamfer049,Box266,Box265,Box264]
FEATURE [Part::Cut] Cut  label="Battery holder 1"
  Base = -> Fusion073
  Tool = -> Fillet031
FEATURE [Part::Box] Box276  label="Cube247"
  AttacherType = Attacher::AttachEngine3D
  Height = 3
  Length = 8
  Placement = pos=(3,32,0) rot=(0,0,1;0rad)
  Width = 8
FEATURE [Part::Box] Box277  label="Cube248"
  AttacherType = Attacher::AttachEngine3D
  Height = 3
  Length = 8
  Placement = pos=(3,32,0) rot=(0,0,1;0rad)
  Width = 8
FEATURE [Part::Chamfer] Chamfer051
  Base = -> Box276
  Edges = 1 edges r=7.9: [Edge5]
  Placement = pos=(0,2,0) rot=(0,0,1;0rad)
FEATURE [Part::Chamfer] Chamfer052
  Base = -> Box277
  Edges = 1 edges r=7.9: [Edge5]
  Placement = pos=(0,2,47) rot=(0,0,1;0rad)
FEATURE [Part::Box] Box278  label="Cube249"
  AttacherType = Attacher::AttachEngine3D
  Height = 50
  Length = 3
  Placement = pos=(0,37,0) rot=(0,0,1;0rad)
  Width = 5
FEATURE [Part::Box] Box279  label="Cube250"
  AttacherType = Attacher::AttachEngine3D
  Height = 10
  Length = 3
  Width = 42
FEATURE [Part::Box] Box280  label="Cube251"
  AttacherType = Attacher::AttachEngine3D
  Height = 10
  Length = 3
  Placement = pos=(0,0,40) rot=(0,0,1;0rad)
  Width = 42
FEATURE [Part::MultiFuse] Fusion074
  Shapes = -> [Chamfer051,Chamfer052,Box278,Box280,Box279]
FEATURE [Part::Box] Box281  label="Cube252"
  AttacherType = Attacher::AttachEngine3D
  Height = 45
  Length = 97
  Width = 22
FEATURE [Part::Fillet] Fillet032  label="Battery pack002"
  Base = -> Box281
  Edges = 4 edges r=10.9: [Edge9,Edge10,Edge11,Edge12]
  Placement = pos=(0,0,2.5) rot=(0,0,1;0rad)
FEATURE [Part::Cut] Cut199  label="Battery holder 2"
  Base = -> Fusion074
  Placement = pos=(69.5,0,0) rot=(0,0,1;0rad)
  Tool = -> Fillet032
